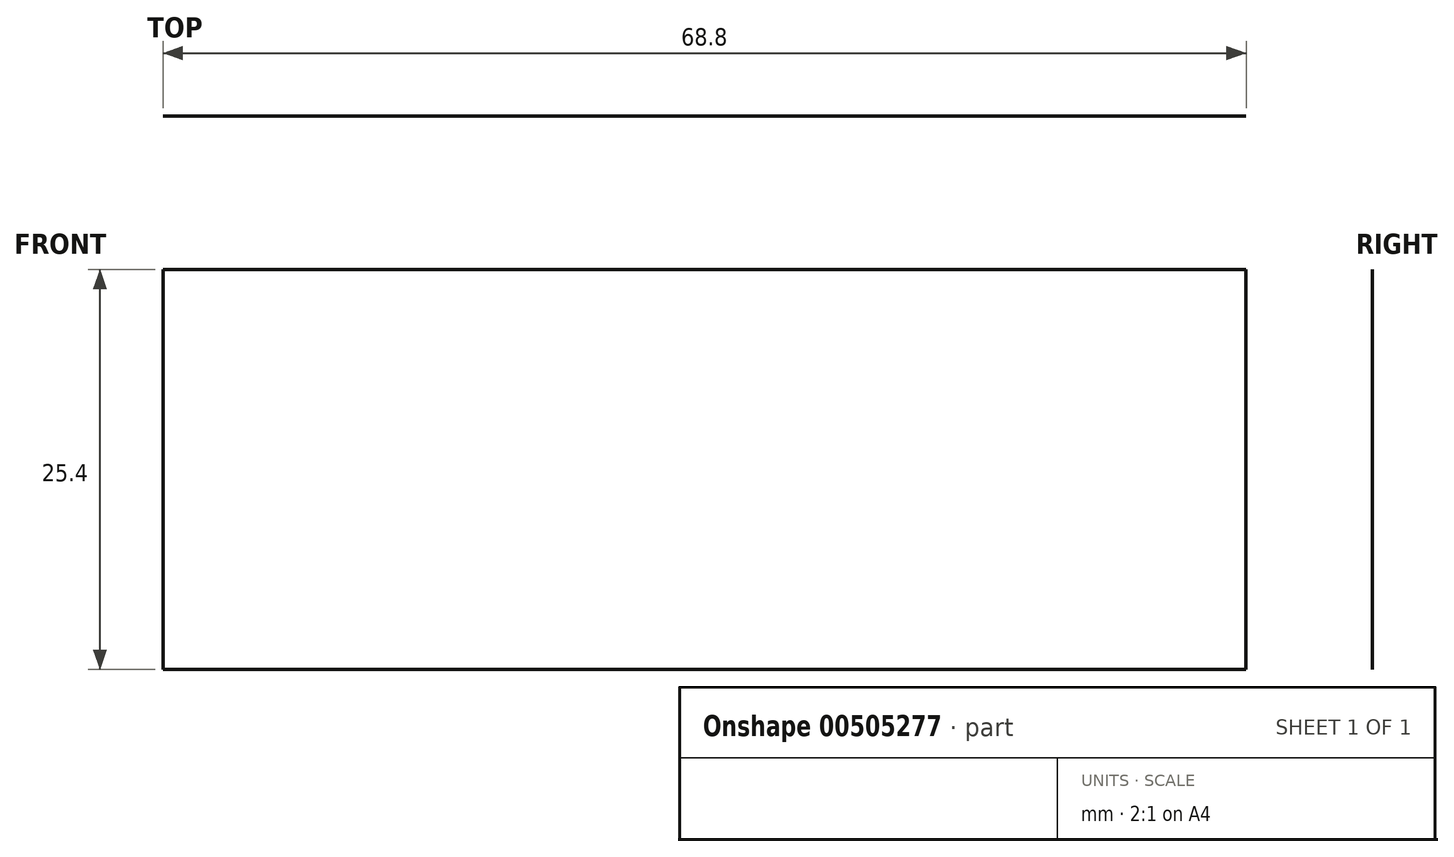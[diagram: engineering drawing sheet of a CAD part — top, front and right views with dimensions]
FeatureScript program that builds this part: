
annotation { "Feature Type Name" : "Feature", "Feature Type Description" : "" }
export const myFeature = defineFeature(function(context is Context, id is Id, definition is map)
    precondition{}
    {
        {
            var Q0;
            Q0=qCreatedBy(makeId("Top.planeOp"),FACE);
            var sketch = newSketch(context, id + "F0", { "sketchPlane" : qUnion([Q0])});
            skLineSegment(sketch, "E0.bottom", {"start": v(0, 117.46) * mm, "end": v(68.8, 117.46) * mm});
            skLineSegment(sketch, "E0.top", {"start": v(0, 0) * mm, "end": v(68.8, 0) * mm});
            skLineSegment(sketch, "E0.left", {"start": v(0, 117.46) * mm, "end": v(0, 0) * mm});
            skLineSegment(sketch, "E0.right", {"start": v(68.8, 117.46) * mm, "end": v(68.8, 0) * mm});
            skSolve(sketch);
        }
        {
            var Q0;
            Q0=sQuery(id+"F0.wireOp",EDGE,"E0.bottom");
            extrude(context, id + "F1", {"bodyType" : ToolBodyType.SURFACE, "surfaceEntities" : qUnion([Q0]), "depth" : 25.4 * mm});
        }
    });
